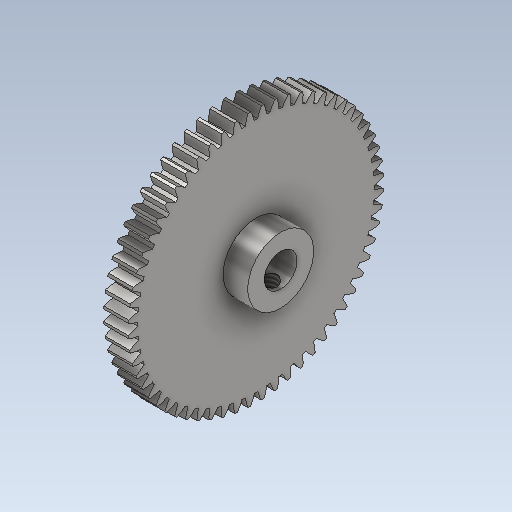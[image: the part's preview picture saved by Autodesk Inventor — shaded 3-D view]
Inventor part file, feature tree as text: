
AUTODESK INVENTOR PART (.ipt)
format: ipt  version: 2023 (Build 270158000, 158)  size: 495,616 bytes
history: native  units: in
note: dims shown in document units (in); Inventor stores cm internally (conversion verified against a paired STEP export)
features: other x3, sketch x2
ambient origin geometry x8: Origin, YZ Plane, XZ Plane, XY Plane, X Axis, Y Axis, Z Axis, Center Point
bodies: Solid1 (feature_tree)
feature tree (5):
  other  "CH-1-01-60T_Idler.ipt"
  other  "Solid1::CH-1-01-60T_Idler.ipt"
  other  "TaggingFeature1"
  sketch  "Sketch3"  dims[d0=0.3937in]
  sketch  "Sketch4"
